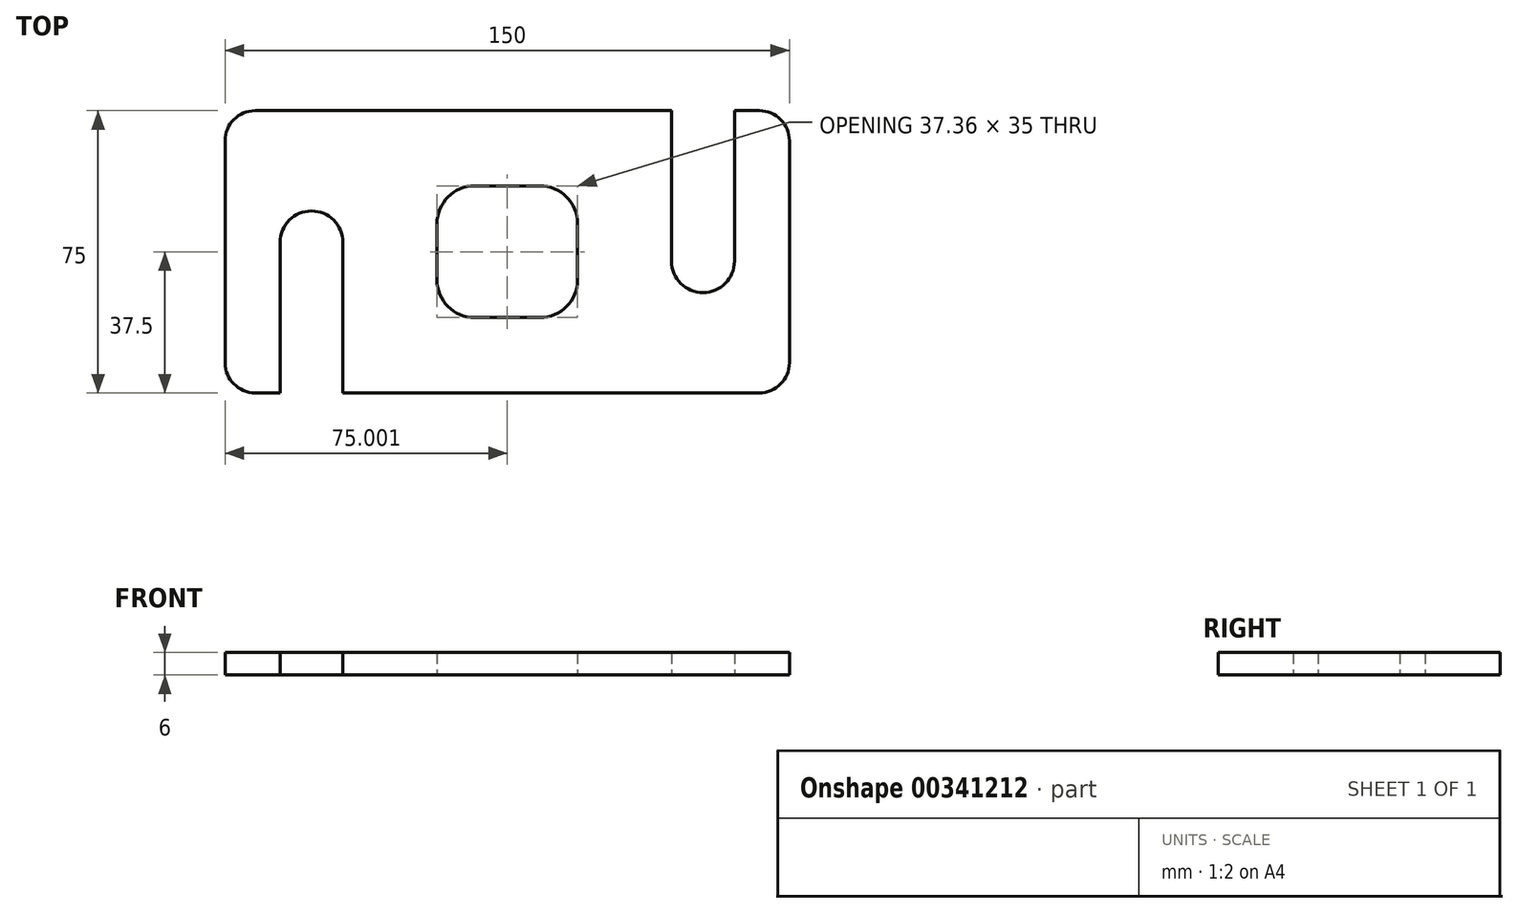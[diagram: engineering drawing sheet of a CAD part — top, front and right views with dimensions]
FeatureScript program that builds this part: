
annotation { "Feature Type Name" : "Feature", "Feature Type Description" : "" }
export const myFeature = defineFeature(function(context is Context, id is Id, definition is map)
    precondition{}
    {
        {
            var Q0;
            Q0=qCreatedBy(makeId("Top.planeOp"),FACE);
            var sketch = newSketch(context, id + "F0", { "sketchPlane" : qUnion([Q0])});
            skLineSegment(sketch, "E0.bottom", {"start": v(8, 0) * mm, "end": v(14.62, 0) * mm});
            skLineSegment(sketch, "E0.top", {"start": v(8, 75) * mm, "end": v(118.68, 75) * mm});
            skLineSegment(sketch, "E0.left", {"start": v(0, 8) * mm, "end": v(0, 67) * mm});
            skLineSegment(sketch, "E0.right", {"start": v(150, 8) * mm, "end": v(150, 67) * mm});
            skPoint(sketch, "E1.visualSharp", {"position": v(0, 75) * mm});
            skArc(sketch, "E1.filletArc", {"start": v(8, 75) * mm, "mid": v(2.34, 72.66) * mm, "end": v(0, 67) * mm});
            skPoint(sketch, "E2.visualSharp", {"position": v(150, 75) * mm});
            skArc(sketch, "E2.filletArc", {"start": v(150, 67) * mm, "mid": v(147.66, 72.66) * mm, "end": v(142, 75) * mm});
            skPoint(sketch, "E3.visualSharp", {"position": v(150, 0) * mm});
            skArc(sketch, "E3.filletArc", {"start": v(142, 0) * mm, "mid": v(147.66, 2.34) * mm, "end": v(150, 8) * mm});
            skPoint(sketch, "E4.visualSharp", {"position": v(0, 0) * mm});
            skArc(sketch, "E4.filletArc", {"start": v(0, 8) * mm, "mid": v(2.34, 2.34) * mm, "end": v(8, 0) * mm});
            skLineSegment(sketch, "E5", {"start": v(14.62, 0) * mm, "end": v(14.62, 40) * mm});
            skArc(sketch, "E6", {"start": v(14.62, 40) * mm, "mid": v(22.97, 48.35) * mm, "end": v(31.32, 40) * mm});
            skLineSegment(sketch, "E7", {"start": v(31.32, 40) * mm, "end": v(31.32, 0) * mm});
            skPoint(sketch, "E8", {"position": v(14.62, 0) * mm});
            skPoint(sketch, "E9", {"position": v(31.32, 0) * mm});
            skLineSegment(sketch, "E10.trimOffspring", {"start": v(31.32, 0) * mm, "end": v(142, 0) * mm});
            skLineSegment(sketch, "E11", {"start": v(135.4, 75) * mm, "end": v(135.4, 35) * mm});
            skArc(sketch, "E12", {"start": v(135.4, 35) * mm, "mid": v(127.04, 26.64) * mm, "end": v(118.68, 35) * mm});
            skLineSegment(sketch, "E13", {"start": v(118.68, 35) * mm, "end": v(118.68, 75) * mm});
            skLineSegment(sketch, "E14.bottom", {"start": v(66.32, 55) * mm, "end": v(83.68, 55) * mm});
            skLineSegment(sketch, "E14.top", {"start": v(66.32, 20) * mm, "end": v(83.68, 20) * mm});
            skLineSegment(sketch, "E14.left", {"start": v(56.32, 45) * mm, "end": v(56.32, 30) * mm});
            skLineSegment(sketch, "E14.right", {"start": v(93.68, 45) * mm, "end": v(93.68, 30) * mm});
            skPoint(sketch, "E15.visualSharp", {"position": v(56.32, 55) * mm});
            skArc(sketch, "E15.filletArc", {"start": v(66.32, 55) * mm, "mid": v(59.25, 52.07) * mm, "end": v(56.32, 45) * mm});
            skPoint(sketch, "E16.visualSharp", {"position": v(93.68, 55) * mm});
            skArc(sketch, "E16.filletArc", {"start": v(93.68, 45) * mm, "mid": v(90.75, 52.07) * mm, "end": v(83.68, 55) * mm});
            skPoint(sketch, "E17.visualSharp", {"position": v(93.68, 20) * mm});
            skArc(sketch, "E17.filletArc", {"start": v(83.68, 20) * mm, "mid": v(90.75, 22.93) * mm, "end": v(93.68, 30) * mm});
            skPoint(sketch, "E18.visualSharp", {"position": v(56.32, 20) * mm});
            skArc(sketch, "E18.filletArc", {"start": v(56.32, 30) * mm, "mid": v(59.25, 22.93) * mm, "end": v(66.32, 20) * mm});
            skLineSegment(sketch, "E19.trimOffspring", {"start": v(135.4, 75) * mm, "end": v(142, 75) * mm});
            skSolve(sketch);
        }
        {
            var Q0;
            Q0=makeQuery(id+"F0.imprint","IMPRINT",FACE,{"disambiguationData":[TD([[makeQuery(id+"F0.imprint","IMPRINT",EDGE,{"derivedFrom":sQuery(id+"F0.wireOp",EDGE,"E0.bottom")}),1.0]])]});
            extrude(context, id + "F1", {"entities" : qUnion([Q0]), "depth" : 6 * mm});
        }
    });
